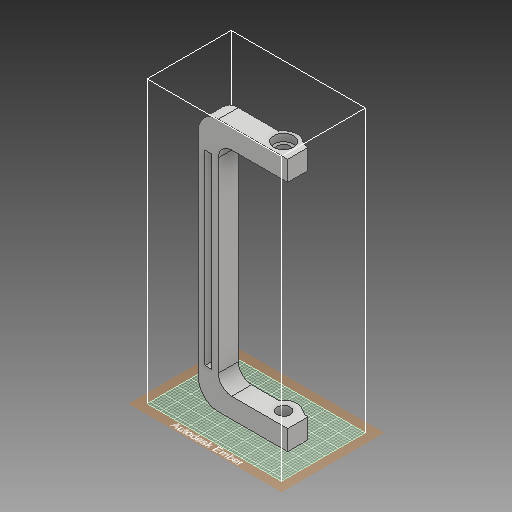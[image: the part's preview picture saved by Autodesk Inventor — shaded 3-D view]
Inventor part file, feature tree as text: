
AUTODESK INVENTOR PART (.ipt)
format: ipt  version: 2018 (Build 220112000, 112)  size: 408,576 bytes
history: native  units: in
note: dims shown in document units (in); Inventor stores cm internally (conversion verified against a paired STEP export)
features: sketch x19, extrude x11, fillet x6, hole x3, plane x1, mirror x1
ambient origin geometry x8: Origin, YZ Plane, XZ Plane, XY Plane, X Axis, Y Axis, Z Axis, Center Point
bodies: Solid1 (feature_tree)
feature tree (41):
  extrude  "Extrusion1"  Depth=0.375in
  sketch  "Sketch2"  dims[d3=0.375in d4=0.5in d5=0.375in d6=0.0in]
  extrude  "Extrusion2"  Depth=0.375in
  fillet  "Fillet1"  Radius=0.375in
  extrude  "Extrusion3"  Depth=0.375in
  extrude  "Extrusion4"  Depth=0.25in
  plane  "Work Plane1"
  mirror  "Mirror1"
  fillet  "Fillet2"  Radius=0.24in
  extrude  "Extrusion5"  Depth=0.375in
  sketch  "Sketch6"  dims[d17=1.0in d18=0.0in d19=0.24in d20=0.0in]
  extrude  "Extrusion6"  Depth=0.24in TaperAngle=0.0deg
  extrude  "Extrusion7"  Depth=0.375in
  fillet  "Fillet3"  Radius=0.25in
  fillet  "Fillet4"  Radius=0.375in
  fillet  "Fillet5"  Radius=0.25in
  fillet  "Fillet6"  Radius=0.125in
  sketch  "Sketch9"  dims[d30=0.125in d31=0.125in]
  extrude  "Extrusion8"  Depth=0.035in
  sketch  "Sketch11"  dims[d35=0.2in]
  sketch  "Sketch12"  dims[d36=0.2in d37=0.75in d38=0.375in d39=0.25in d40=0.5635in d41=0.35in d42=0.0in]
  hole  "Hole1"  [1 undecoded]
  hole  "Hole2"  [1 undecoded]
  sketch  "Sketch14"  dims[d51=3.5in d52=0.375in d53=0.0in]
  extrude  "Extrusion9"  Depth=0.125in
  extrude  "Extrusion10"  Depth=0.375in TaperAngle=0.0deg
  sketch  "Sketch17"  dims[d60=0.25in]
  extrude  "Extrusion11"  Depth=0.25in
  hole  "Hole3"  [1 undecoded]
  sketch  "Sketch1"  dims[d0=1.3in d1=0.375in]
  sketch  "Sketch3"  dims[d7=0.375in d8=0.0in d9=0.375in]
  sketch  "Sketch4"  dims[d10=0.24in d11=0.0in d12=0.25in d13=0.24in d14=0.0in]
  sketch  "Sketch5"  dims[d15=2.0in d16=0.375in]
  sketch  "Sketch7"  dims[d21=0.375in d22=0.0in d23=0.375in d24=0.25in d25=0.375in d26=0.25in d27=0.125in]
  sketch  "Sketch8"  dims[d28=0.035in d29=0.035in]
  sketch  "Sketch10"  dims[d32=4.375in d33=0.0in d34=0.2in]
  sketch  "Sketch13"  dims[d43=0.2in d44=0.75in d45=0.375in d46=0.25in d47=0.5635in d48=0.35in d49=0.0in d50=0.125in]
  sketch  "Sketch15"  dims[d54=1.0in d55=0.0in d56=0.25in]
  sketch  "Sketch16"  dims[d57=0.25in d58=0.5in d59=0.0in]
  sketch  "Sketch18"  dims[d61=0.25in d62=0.75in d63=0.375in d64=0.25in d65=0.5635in d66=0.5in d67=0.0in]
  sketch  "Sketch19"
note: 3 required parameter values undecoded (feature->parameter linkage not recoverable at this tier; creation-order binding heuristic only, values carry confidence <= 0.55)
